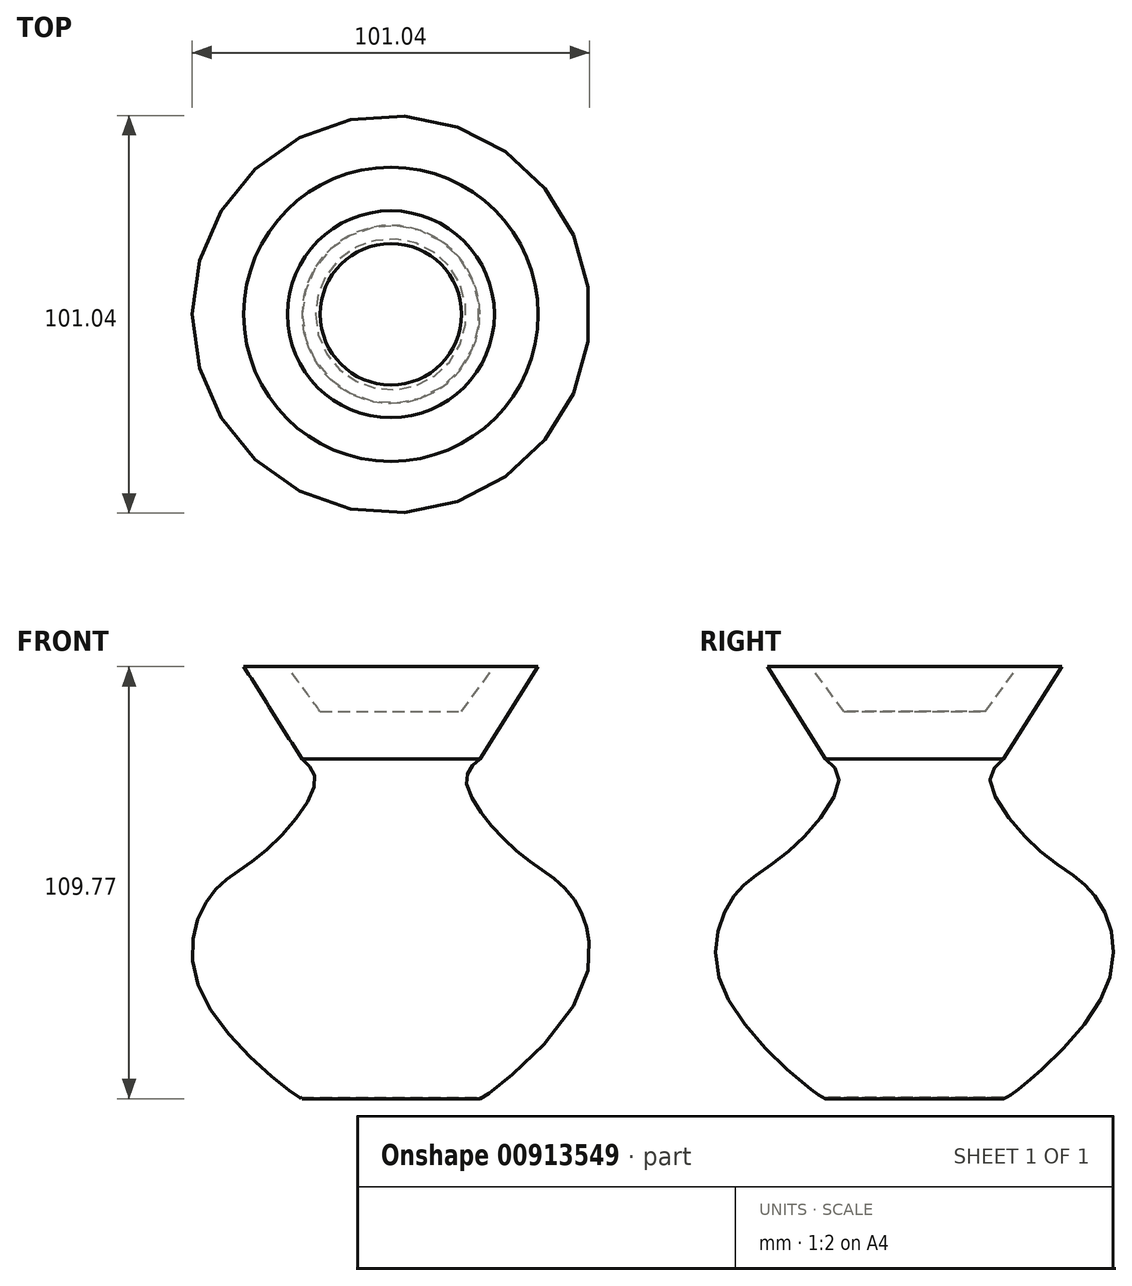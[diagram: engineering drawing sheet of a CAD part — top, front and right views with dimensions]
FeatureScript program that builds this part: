
annotation { "Feature Type Name" : "Feature", "Feature Type Description" : "" }
export const myFeature = defineFeature(function(context is Context, id is Id, definition is map)
    precondition{}
    {
        {
            var Q0;
            Q0=qCreatedBy(makeId("Front.planeOp"),FACE);
            var sketch = newSketch(context, id + "F0", { "sketchPlane" : qUnion([Q0])});
            skLineSegment(sketch, "E0", {"start": v(0, 42.78) * mm, "end": v(17.96, 42.78) * mm});
            skLineSegment(sketch, "E1", {"start": v(17.96, 42.78) * mm, "end": v(26.28, 54.19) * mm});
            skLineSegment(sketch, "E2", {"start": v(26.28, 54.19) * mm, "end": v(37.38, 54.19) * mm});
            skLineSegment(sketch, "E3", {"start": v(37.38, 54.19) * mm, "end": v(22.58, 30.76) * mm});
            skFitSpline(sketch, "E4", {"points": [v(22.58, 30.76) * mm, v(19.2, 24.9) * mm, v(33.07, 6.4) * mm, v(45.4, -3.47) * mm, v(47.87, -29.37) * mm, v(22.58, -55.58) * mm, v(22.58, -55.27) * mm], "startDerivative": vector(-48.25, -42.39) * mm, "endDerivative": vector(6, 17.77) * mm});
            skLineSegment(sketch, "E5", {"start": v(22.58, -55.27) * mm, "end": v(22.58, -63.28) * mm});
            skLineSegment(sketch, "E6", {"start": v(22.58, -63.28) * mm, "end": v(0, -63.28) * mm});
            skLineSegment(sketch, "E7", {"start": v(0, 59.12) * mm, "end": v(0, -67.9) * mm, "construction": true});
            skSolve(sketch);
        }
        {
            var Q0;
            Q0=sQuery(id+"F0.wireOp",EDGE,"E4");
            var Q1;
            Q1=sQuery(id+"F0.wireOp",EDGE,"E3");
            var Q2;
            Q2=sQuery(id+"F0.wireOp",EDGE,"E2");
            var Q3;
            Q3=sQuery(id+"F0.wireOp",EDGE,"E1");
            var Q4;
            Q4=sQuery(id+"F0.wireOp",EDGE,"E0");
            var Q5;
            Q5=sQuery(id+"F0.wireOp",EDGE,"E7");
            revolve(context, id + "F1", {"bodyType" : ToolBodyType.SURFACE, "surfaceOperationType" : NewSurfaceOperationType.NEW, "surfaceEntities" : qUnion([Q0, Q1, Q2, Q3, Q4]), "axis" : qUnion([Q5]), "revolveType" : RevolveType.FULL});
        }
    });
